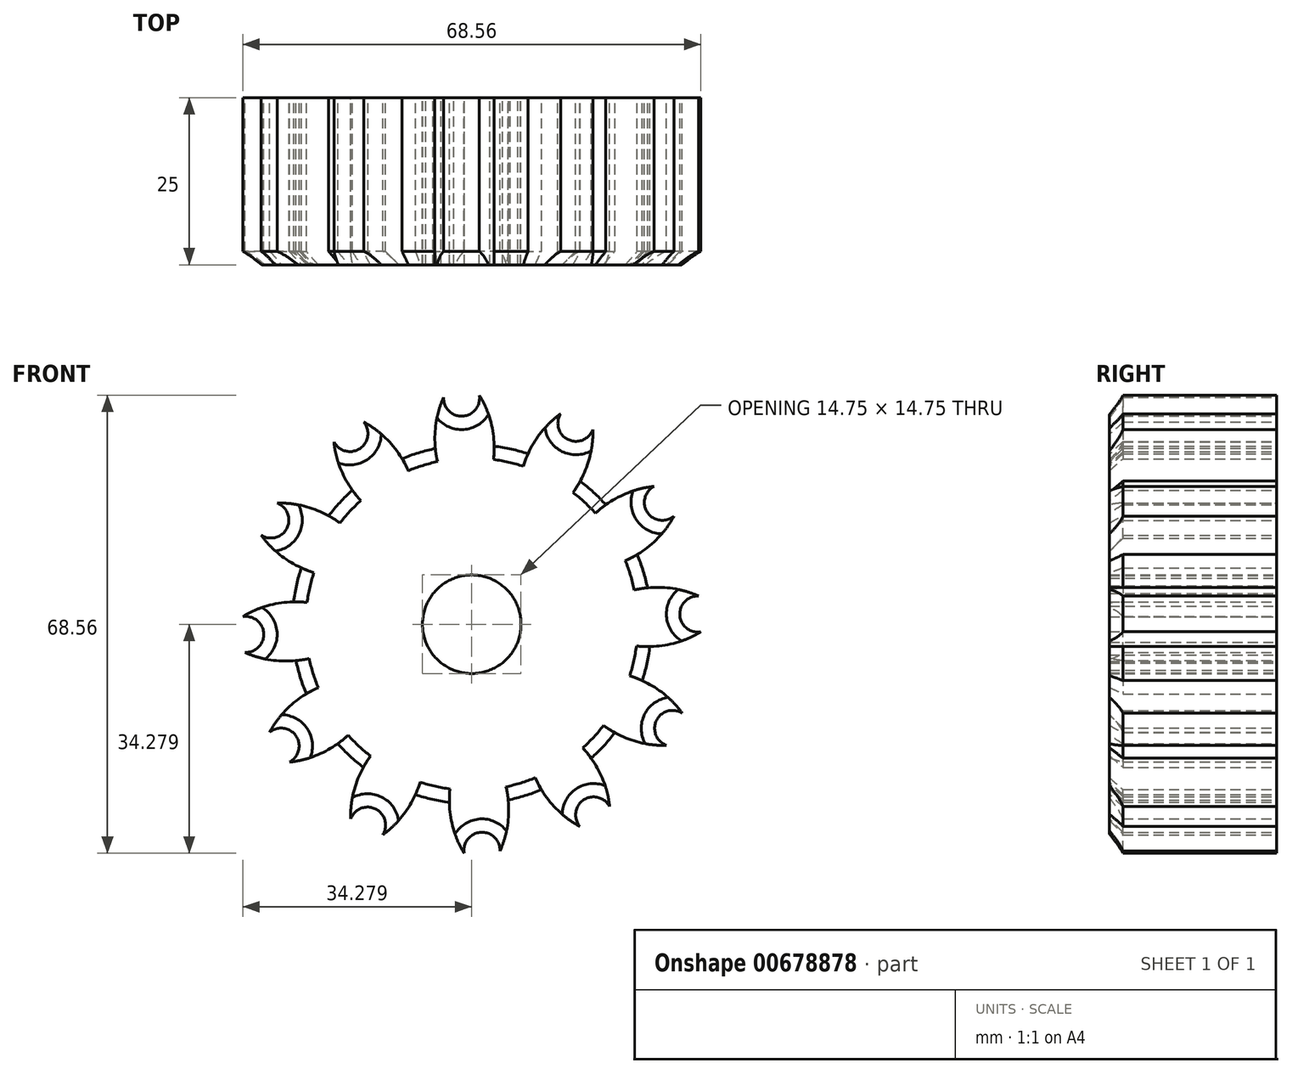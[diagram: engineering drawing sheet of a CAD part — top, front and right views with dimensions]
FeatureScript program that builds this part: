
annotation { "Feature Type Name" : "Feature", "Feature Type Description" : "" }
export const myFeature = defineFeature(function(context is Context, id is Id, definition is map)
    precondition{}
    {
        {
            var Q0;
            Q0=qCreatedBy(makeId("Front.planeOp"),FACE);
            var sketch = newSketch(context, id + "F0", { "sketchPlane" : qUnion([Q0])});
            skCircle(sketch, "E0", {"center": v(6.7, -22.54) * mm, "radius": 26.86 * mm});
            skCircle(sketch, "E1", {"center": v(6.7, -22.54) * mm, "radius": 29.34 * mm, "construction": true});
            skCircle(sketch, "E2", {"center": v(6.7, -22.54) * mm, "radius": 31.75 * mm, "construction": true});
            skLineSegment(sketch, "E3", {"start": v(6.7, -22.54) * mm, "end": v(6.7, 79.1) * mm, "construction": true});
            skLineSegment(sketch, "E4", {"start": v(6.7, -22.54) * mm, "end": v(-0.35, 84.96) * mm, "construction": true});
            skLineSegment(sketch, "E5", {"start": v(6.7, 6.8) * mm, "end": v(-78.45, 6.8) * mm, "construction": true});
            skLineSegment(sketch, "E6", {"start": v(6.7, 6.8) * mm, "end": v(-74.14, -22.63) * mm, "construction": true});
            skCircle(sketch, "E7", {"center": v(6.7, -22.54) * mm, "radius": 27.57 * mm, "construction": true});
            skCircle(sketch, "E8", {"center": v(6.7, 6.8) * mm, "radius": 14.6 * mm, "construction": true});
            skCircle(sketch, "E9", {"center": v(-7.03, 1.8) * mm, "radius": 14.6 * mm, "construction": true});
            skCircle(sketch, "E10", {"center": v(6.7, -22.54) * mm, "radius": 36.8 * mm});
            skArc(sketch, "E11", {"start": v(9.17, 8.96) * mm, "mid": v(7.98, 11.48) * mm, "end": v(6.31, 13.72) * mm});
            skArc(sketch, "E12", {"start": v(10.05, 4) * mm, "mid": v(9.81, 6.51) * mm, "end": v(9.17, 8.96) * mm});
            skArc(sketch, "E13.MirrorCS", {"start": v(1.51, 8.45) * mm, "mid": v(2.36, 11.11) * mm, "end": v(3.72, 13.55) * mm});
            skArc(sketch, "E14.MirrorCS", {"start": v(1.28, 3.42) * mm, "mid": v(1.2, 5.95) * mm, "end": v(1.51, 8.45) * mm});
            skArc(sketch, "E15", {"start": v(3.72, 13.55) * mm, "mid": v(5.35, 8.6) * mm, "end": v(6.31, 13.72) * mm});
            skCircle(sketch, "E16", {"center": v(6.49, -22.52) * mm, "radius": 7.59 * mm});
            skSolve(sketch);
        }
        {
            var Q0;
            {var subQ0=sQuery(id+"F0.wireOp",EDGE,"E0");var subQ1=makeQuery(id+"F0.imprint","INTERSECT",VERTEX,{"derivedFrom":[subQ0,sQuery(id+"F0.wireOp",EDGE,"E12")]});Q0=makeQuery(id+"F0.imprint","IMPRINT",FACE,{"disambiguationData":[TD([[makeQuery(id+"F0.imprint","IMPRINT",EDGE,{"disambiguationData":[TD([[subQ1,-1.0]])],"derivedFrom":subQ0}),1.0]])]});}
            var Q1;
            {var subQ5=sQuery(id+"F0.wireOp",EDGE,"E12");var subQ9=sQuery(id+"F0.wireOp",EDGE,"E0");var subQ10=makeQuery(id+"F0.imprint","INTERSECT",VERTEX,{"derivedFrom":[subQ9,subQ5]});Q1=makeQuery(id+"F0.imprint","IMPRINT",FACE,{"disambiguationData":[TD([[makeQuery(id+"F0.imprint","IMPRINT",EDGE,{"disambiguationData":[TD([[subQ10,-1.0]])],"derivedFrom":subQ9}),-1.0]])]});}
            extrude(context, id + "F1", {"entities" : qUnion([Q0, Q1]), "depth" : 25 * mm, "offsetDistance" : 25 * mm});
        }
        {
            var Q0;
            Q0=makeQuery(id+"F1.opExtrude","SWEPT_BODY",BODY,{"disambiguationData":[OSD([sQuery(id+"F0.wireOp",EDGE,"E0"),sQuery(id+"F0.wireOp",EDGE,"E11"),sQuery(id+"F0.wireOp",EDGE,"E12"),sQuery(id+"F0.wireOp",EDGE,"E13.MirrorCS"),sQuery(id+"F0.wireOp",EDGE,"E14.MirrorCS"),sQuery(id+"F0.wireOp",EDGE,"E15")])]});
            var Q1;
            Q1=makeQuery(id+"F1.opExtrude","SWEPT_FACE",FACE,{"disambiguationData":[OSD([sQuery(id+"F0.wireOp",EDGE,"E0")])]});
            circularPattern(context, id + "F2", {"operationType" : NewBodyOperationType.ADD, "entities" : qUnion([Q0]), "axis" : qUnion([Q1]), "angle" : 360 * degree, "instanceCount" : 12, "equalSpace" : true});
        }
        {
            var Q0;
            Q0=makeQuery(id+"F2.opPattern","COPY",EDGE,{"derivedFrom":makeQuery(id+"F1.opExtrude","CAP_EDGE",EDGE,{"disambiguationData":[OSD([sQuery(id+"F0.wireOp",EDGE,"E15")])],"isStart":false}),"instanceName":"11"});
            var Q1;
            Q1=makeQuery(id+"F1.opExtrude","CAP_EDGE",EDGE,{"disambiguationData":[OSD([sQuery(id+"F0.wireOp",EDGE,"E15")])],"isStart":false});
            var Q2;
            Q2=makeQuery(id+"F2.opPattern","COPY",EDGE,{"derivedFrom":makeQuery(id+"F1.opExtrude","CAP_EDGE",EDGE,{"disambiguationData":[OSD([sQuery(id+"F0.wireOp",EDGE,"E15")])],"isStart":false}),"instanceName":"1"});
            var Q3;
            Q3=makeQuery(id+"F2.opPattern","COPY",EDGE,{"derivedFrom":makeQuery(id+"F1.opExtrude","CAP_EDGE",EDGE,{"disambiguationData":[OSD([sQuery(id+"F0.wireOp",EDGE,"E15")])],"isStart":false}),"instanceName":"2"});
            var Q4;
            Q4=makeQuery(id+"F2.opPattern","COPY",EDGE,{"derivedFrom":makeQuery(id+"F1.opExtrude","CAP_EDGE",EDGE,{"disambiguationData":[OSD([sQuery(id+"F0.wireOp",EDGE,"E15")])],"isStart":false}),"instanceName":"3"});
            var Q5;
            Q5=makeQuery(id+"F2.opPattern","COPY",EDGE,{"derivedFrom":makeQuery(id+"F1.opExtrude","CAP_EDGE",EDGE,{"disambiguationData":[OSD([sQuery(id+"F0.wireOp",EDGE,"E15")])],"isStart":false}),"instanceName":"4"});
            var Q6;
            Q6=makeQuery(id+"F2.opPattern","COPY",EDGE,{"derivedFrom":makeQuery(id+"F1.opExtrude","CAP_EDGE",EDGE,{"disambiguationData":[OSD([sQuery(id+"F0.wireOp",EDGE,"E15")])],"isStart":false}),"instanceName":"5"});
            var Q7;
            Q7=makeQuery(id+"F2.opPattern","COPY",EDGE,{"derivedFrom":makeQuery(id+"F1.opExtrude","CAP_EDGE",EDGE,{"disambiguationData":[OSD([sQuery(id+"F0.wireOp",EDGE,"E15")])],"isStart":false}),"instanceName":"6"});
            var Q8;
            Q8=makeQuery(id+"F2.opPattern","COPY",EDGE,{"derivedFrom":makeQuery(id+"F1.opExtrude","CAP_EDGE",EDGE,{"disambiguationData":[OSD([sQuery(id+"F0.wireOp",EDGE,"E15")])],"isStart":false}),"instanceName":"7"});
            var Q9;
            Q9=makeQuery(id+"F2.opPattern","COPY",EDGE,{"derivedFrom":makeQuery(id+"F1.opExtrude","CAP_EDGE",EDGE,{"disambiguationData":[OSD([sQuery(id+"F0.wireOp",EDGE,"E15")])],"isStart":false}),"instanceName":"8"});
            var Q10;
            Q10=makeQuery(id+"F2.opPattern","COPY",EDGE,{"derivedFrom":makeQuery(id+"F1.opExtrude","CAP_EDGE",EDGE,{"disambiguationData":[OSD([sQuery(id+"F0.wireOp",EDGE,"E15")])],"isStart":false}),"instanceName":"9"});
            var Q11;
            Q11=makeQuery(id+"F2.opPattern","COPY",EDGE,{"derivedFrom":makeQuery(id+"F1.opExtrude","CAP_EDGE",EDGE,{"disambiguationData":[OSD([sQuery(id+"F0.wireOp",EDGE,"E15")])],"isStart":false}),"instanceName":"10"});
            var Q12;
            {var subQ1=sQuery(id+"F0.wireOp",EDGE,"E12");var subQ2=sQuery(id+"F0.wireOp",EDGE,"E0");Q12=makeQuery(id+"F2.boolean.opBoolean","SPLIT",EDGE,{"disambiguationData":[TD([makeQuery(id+"F2.opPattern","COPY",FACE,{"derivedFrom":makeQuery(id+"F1.opExtrude","SWEPT_FACE",FACE,{"disambiguationData":[OSD([subQ1])]}),"instanceName":"10"})])],"derivedFrom":makeQuery(id+"F1.opExtrude","CAP_EDGE",EDGE,{"disambiguationData":[OSD([subQ2])],"isStart":false})});}
            var Q13;
            {var subQ0=sQuery(id+"F0.wireOp",EDGE,"E14.MirrorCS");var subQ2=sQuery(id+"F0.wireOp",EDGE,"E0");Q13=makeQuery(id+"F2.boolean.opBoolean","SPLIT",EDGE,{"disambiguationData":[TD([makeQuery(id+"F1.opExtrude","SWEPT_FACE",FACE,{"disambiguationData":[OSD([subQ0])]})])],"derivedFrom":makeQuery(id+"F1.opExtrude","CAP_EDGE",EDGE,{"disambiguationData":[OSD([subQ2])],"isStart":false})});}
            var Q14;
            {var subQ1=sQuery(id+"F0.wireOp",EDGE,"E12");var subQ2=sQuery(id+"F0.wireOp",EDGE,"E0");Q14=makeQuery(id+"F2.boolean.opBoolean","SPLIT",EDGE,{"disambiguationData":[TD([makeQuery(id+"F2.opPattern","COPY",FACE,{"derivedFrom":makeQuery(id+"F1.opExtrude","SWEPT_FACE",FACE,{"disambiguationData":[OSD([subQ1])]}),"instanceName":"9"})])],"derivedFrom":makeQuery(id+"F1.opExtrude","CAP_EDGE",EDGE,{"disambiguationData":[OSD([subQ2])],"isStart":false})});}
            var Q15;
            {var subQ1=sQuery(id+"F0.wireOp",EDGE,"E12");var subQ2=sQuery(id+"F0.wireOp",EDGE,"E0");Q15=makeQuery(id+"F2.boolean.opBoolean","SPLIT",EDGE,{"disambiguationData":[TD([makeQuery(id+"F1.opExtrude","SWEPT_FACE",FACE,{"disambiguationData":[OSD([subQ1])]})])],"derivedFrom":makeQuery(id+"F1.opExtrude","CAP_EDGE",EDGE,{"disambiguationData":[OSD([subQ2])],"isStart":false})});}
            var Q16;
            {var subQ1=sQuery(id+"F0.wireOp",EDGE,"E12");var subQ2=sQuery(id+"F0.wireOp",EDGE,"E0");Q16=makeQuery(id+"F2.boolean.opBoolean","SPLIT",EDGE,{"disambiguationData":[TD([makeQuery(id+"F2.opPattern","COPY",FACE,{"derivedFrom":makeQuery(id+"F1.opExtrude","SWEPT_FACE",FACE,{"disambiguationData":[OSD([subQ1])]}),"instanceName":"8"})])],"derivedFrom":makeQuery(id+"F1.opExtrude","CAP_EDGE",EDGE,{"disambiguationData":[OSD([subQ2])],"isStart":false})});}
            var Q17;
            {var subQ1=sQuery(id+"F0.wireOp",EDGE,"E12");var subQ2=sQuery(id+"F0.wireOp",EDGE,"E0");Q17=makeQuery(id+"F2.boolean.opBoolean","SPLIT",EDGE,{"disambiguationData":[TD([makeQuery(id+"F2.opPattern","COPY",FACE,{"derivedFrom":makeQuery(id+"F1.opExtrude","SWEPT_FACE",FACE,{"disambiguationData":[OSD([subQ1])]}),"instanceName":"1"})])],"derivedFrom":makeQuery(id+"F1.opExtrude","CAP_EDGE",EDGE,{"disambiguationData":[OSD([subQ2])],"isStart":false})});}
            var Q18;
            {var subQ1=sQuery(id+"F0.wireOp",EDGE,"E12");var subQ2=sQuery(id+"F0.wireOp",EDGE,"E0");Q18=makeQuery(id+"F2.boolean.opBoolean","SPLIT",EDGE,{"disambiguationData":[TD([makeQuery(id+"F2.opPattern","COPY",FACE,{"derivedFrom":makeQuery(id+"F1.opExtrude","SWEPT_FACE",FACE,{"disambiguationData":[OSD([subQ1])]}),"instanceName":"2"})])],"derivedFrom":makeQuery(id+"F1.opExtrude","CAP_EDGE",EDGE,{"disambiguationData":[OSD([subQ2])],"isStart":false})});}
            var Q19;
            {var subQ1=sQuery(id+"F0.wireOp",EDGE,"E12");var subQ2=sQuery(id+"F0.wireOp",EDGE,"E0");Q19=makeQuery(id+"F2.boolean.opBoolean","SPLIT",EDGE,{"disambiguationData":[TD([makeQuery(id+"F2.opPattern","COPY",FACE,{"derivedFrom":makeQuery(id+"F1.opExtrude","SWEPT_FACE",FACE,{"disambiguationData":[OSD([subQ1])]}),"instanceName":"3"})])],"derivedFrom":makeQuery(id+"F1.opExtrude","CAP_EDGE",EDGE,{"disambiguationData":[OSD([subQ2])],"isStart":false})});}
            var Q20;
            {var subQ1=sQuery(id+"F0.wireOp",EDGE,"E12");var subQ2=sQuery(id+"F0.wireOp",EDGE,"E0");Q20=makeQuery(id+"F2.boolean.opBoolean","SPLIT",EDGE,{"disambiguationData":[TD([makeQuery(id+"F2.opPattern","COPY",FACE,{"derivedFrom":makeQuery(id+"F1.opExtrude","SWEPT_FACE",FACE,{"disambiguationData":[OSD([subQ1])]}),"instanceName":"4"})])],"derivedFrom":makeQuery(id+"F1.opExtrude","CAP_EDGE",EDGE,{"disambiguationData":[OSD([subQ2])],"isStart":false})});}
            var Q21;
            {var subQ1=sQuery(id+"F0.wireOp",EDGE,"E12");var subQ2=sQuery(id+"F0.wireOp",EDGE,"E0");Q21=makeQuery(id+"F2.boolean.opBoolean","SPLIT",EDGE,{"disambiguationData":[TD([makeQuery(id+"F2.opPattern","COPY",FACE,{"derivedFrom":makeQuery(id+"F1.opExtrude","SWEPT_FACE",FACE,{"disambiguationData":[OSD([subQ1])]}),"instanceName":"5"})])],"derivedFrom":makeQuery(id+"F1.opExtrude","CAP_EDGE",EDGE,{"disambiguationData":[OSD([subQ2])],"isStart":false})});}
            var Q22;
            {var subQ1=sQuery(id+"F0.wireOp",EDGE,"E12");var subQ2=sQuery(id+"F0.wireOp",EDGE,"E0");Q22=makeQuery(id+"F2.boolean.opBoolean","SPLIT",EDGE,{"disambiguationData":[TD([makeQuery(id+"F2.opPattern","COPY",FACE,{"derivedFrom":makeQuery(id+"F1.opExtrude","SWEPT_FACE",FACE,{"disambiguationData":[OSD([subQ1])]}),"instanceName":"6"})])],"derivedFrom":makeQuery(id+"F1.opExtrude","CAP_EDGE",EDGE,{"disambiguationData":[OSD([subQ2])],"isStart":false})});}
            var Q23;
            {var subQ1=sQuery(id+"F0.wireOp",EDGE,"E12");var subQ2=sQuery(id+"F0.wireOp",EDGE,"E0");Q23=makeQuery(id+"F2.boolean.opBoolean","SPLIT",EDGE,{"disambiguationData":[TD([makeQuery(id+"F2.opPattern","COPY",FACE,{"derivedFrom":makeQuery(id+"F1.opExtrude","SWEPT_FACE",FACE,{"disambiguationData":[OSD([subQ1])]}),"instanceName":"7"})])],"derivedFrom":makeQuery(id+"F1.opExtrude","CAP_EDGE",EDGE,{"disambiguationData":[OSD([subQ2])],"isStart":false})});}
            chamfer(context, id + "F3", {"entities" : qUnion([Q0, Q1, Q2, Q3, Q4, Q5, Q6, Q7, Q8, Q9, Q10, Q11, Q12, Q13, Q14, Q15, Q16, Q17, Q18, Q19, Q20, Q21, Q22, Q23]), "width" : 2 * mm, "tangentPropagation" : true});
        }
    });
